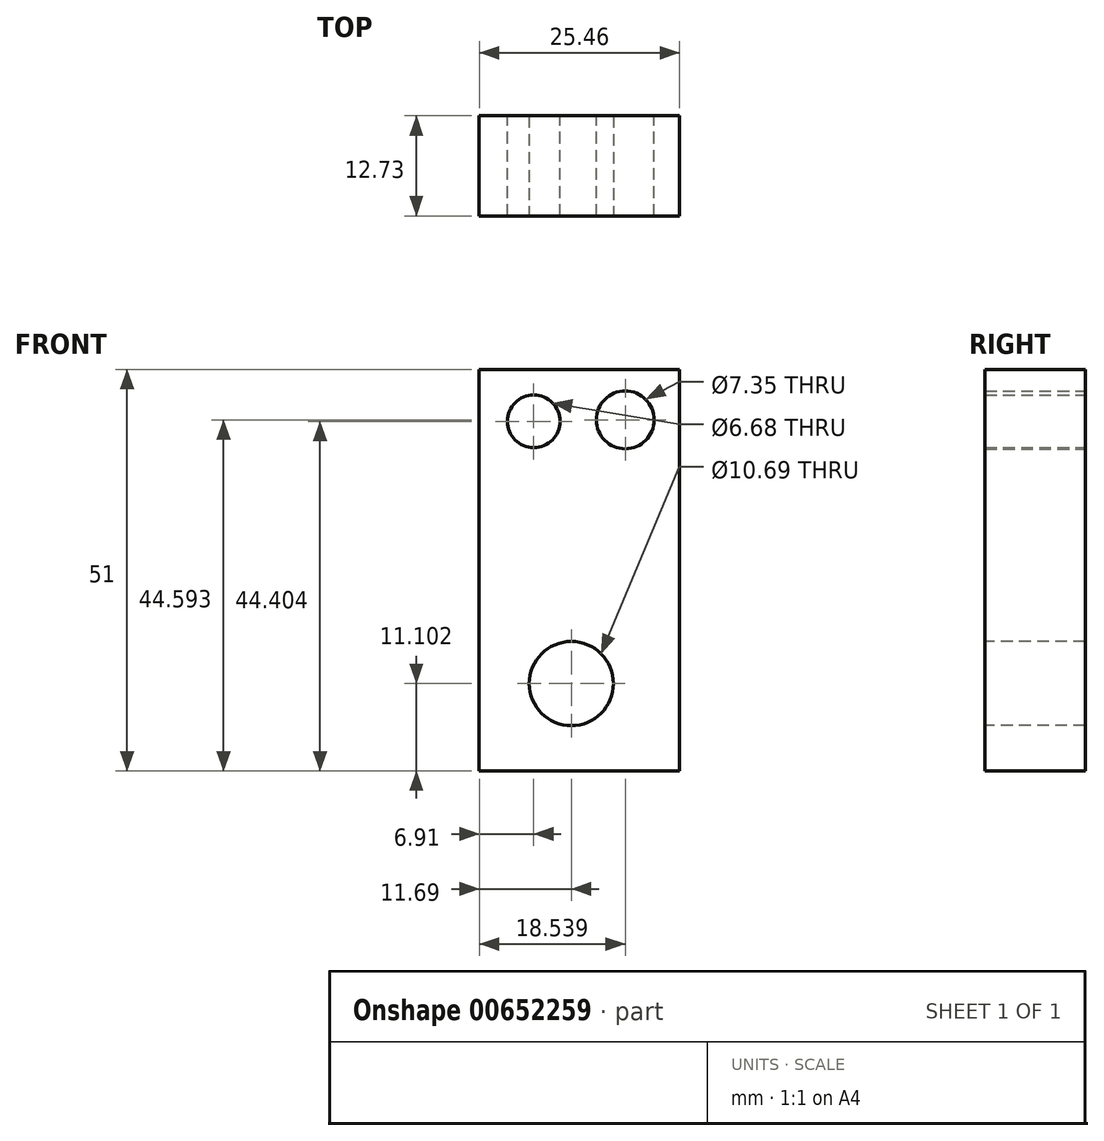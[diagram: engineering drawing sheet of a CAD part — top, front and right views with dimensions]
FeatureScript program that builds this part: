
annotation { "Feature Type Name" : "Feature", "Feature Type Description" : "" }
export const myFeature = defineFeature(function(context is Context, id is Id, definition is map)
    precondition{}
    {
        {
            var Q0;
            Q0=qCreatedBy(makeId("Top.planeOp"),FACE);
            var sketch = newSketch(context, id + "F0", { "sketchPlane" : qUnion([Q0])});
            skLineSegment(sketch, "E0.bottom", {"start": v(-11.7, -5.18) * mm, "end": v(13.77, -5.18) * mm});
            skLineSegment(sketch, "E0.top", {"start": v(-11.7, 7.55) * mm, "end": v(13.77, 7.55) * mm});
            skLineSegment(sketch, "E0.left", {"start": v(-11.7, -5.18) * mm, "end": v(-11.7, 7.55) * mm});
            skLineSegment(sketch, "E0.right", {"start": v(13.77, -5.18) * mm, "end": v(13.77, 7.55) * mm});
            skSolve(sketch);
        }
        {
            var Q0;
            Q0=makeQuery(id+"F0.imprint","IMPRINT",FACE,{"disambiguationData":[TD([[makeQuery(id+"F0.imprint","IMPRINT",EDGE,{"derivedFrom":sQuery(id+"F0.wireOp",EDGE,"E0.bottom")}),1.0]])]});
            var Q1;
            Q1 = qSketchRegion(id + "F2", true);
            extrude(context, id + "F1", {"entities" : qUnion([Q0, Q1]), "depth" : 51 * mm, "offsetDistance" : 25 * mm});
        }
        {
            var Q0;
            Q0=makeQuery(id+"F1.opExtrude","SWEPT_FACE",FACE,{"disambiguationData":[OSD([sQuery(id+"F0.wireOp",EDGE,"E0.top")])]});
            var sketch = newSketch(context, id + "F2", { "sketchPlane" : qUnion([Q0])});
            skCircle(sketch, "E1", {"center": v(-6.85, 44.6) * mm, "radius": 3.68 * mm});
            skSolve(sketch);
        }
        {
            var Q0;
            Q0 = qSketchRegion(id + "F2", true);
            extrude(context, id + "F3", {"entities" : qUnion([Q0]), "operationType" : NewBodyOperationType.REMOVE, "oppositeDirection" : true, "depth" : 25 * mm, "offsetDistance" : 25 * mm});
        }
        {
            var Q0;
            Q0=makeQuery(id+"F1.opExtrude","SWEPT_FACE",FACE,{"disambiguationData":[OSD([sQuery(id+"F0.wireOp",EDGE,"E0.top")])]});
            var sketch = newSketch(context, id + "F4", { "sketchPlane" : qUnion([Q0])});
            skCircle(sketch, "E2", {"center": v(4.78, 44.4) * mm, "radius": 3.34 * mm});
            skSolve(sketch);
        }
        {
            var Q0;
            Q0 = qSketchRegion(id + "F4", true);
            extrude(context, id + "F5", {"entities" : qUnion([Q0]), "operationType" : NewBodyOperationType.REMOVE, "oppositeDirection" : true, "depth" : 25 * mm, "offsetDistance" : 25 * mm});
        }
        {
            var Q0;
            Q0=makeQuery(id+"F1.opExtrude","SWEPT_FACE",FACE,{"disambiguationData":[OSD([sQuery(id+"F0.wireOp",EDGE,"E0.bottom")])]});
            var sketch = newSketch(context, id + "F6", { "sketchPlane" : qUnion([Q0])});
            skCircle(sketch, "E3", {"center": v(0, 11.1) * mm, "radius": 5.35 * mm});
            skSolve(sketch);
        }
        {
            var Q0;
            Q0 = qSketchRegion(id + "F6", true);
            extrude(context, id + "F7", {"entities" : qUnion([Q0]), "operationType" : NewBodyOperationType.REMOVE, "oppositeDirection" : true, "depth" : 25 * mm, "offsetDistance" : 25 * mm});
        }
    });
